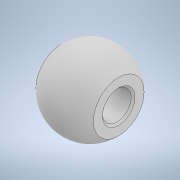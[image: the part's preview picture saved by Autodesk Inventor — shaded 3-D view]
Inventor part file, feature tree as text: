
AUTODESK INVENTOR PART (.ipt)
format: ipt  version: 2020 (Build 240168000, 168)  size: 138,752 bytes
history: native  units: mm
features: sketch x3, extrude x2, revolve x1, chamfer x1, projected_geometry x1
ambient origin geometry x8: Origin, YZ Plane, XZ Plane, XY Plane, X Axis, Y Axis, Z Axis, Center Point
bodies: Solid1 (feature_tree)
feature tree (8):
  revolve  "Revolution1"  Angle=90.0deg
  extrude  "Extrusion1"  Depth=3.0mm
  extrude  "Extrusion2"  Depth=3.0mm
  chamfer  "Chamfer1"  Distance=10.0mm
  sketch  "Sketch1"  dims[d0=8.0mm d1=90.0deg]
  sketch  "Sketch2"  dims[d2=3.0mm d3=3.0mm]
  sketch  "Sketch3"  dims[d4=10.0mm d5=0.0mm d6=3.0mm d7=10.0mm d8=0.0mm d9=0.2mm d10=2.0mm d11=45.0deg]
  projected_geometry  "Projected Loop1"
